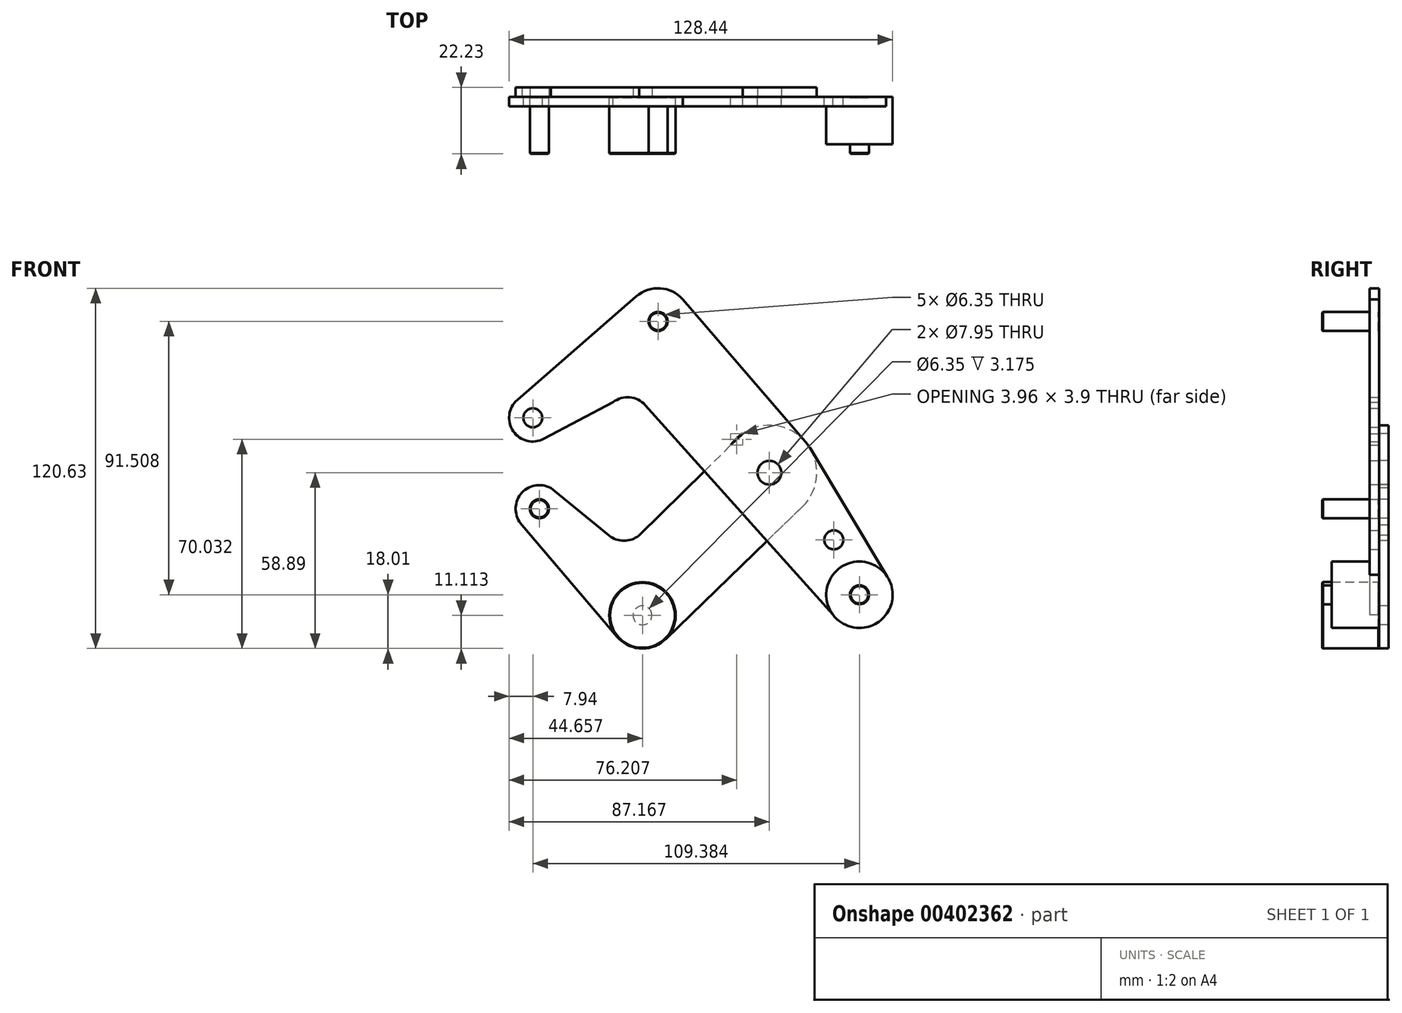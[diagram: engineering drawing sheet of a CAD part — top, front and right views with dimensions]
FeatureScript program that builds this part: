
annotation { "Feature Type Name" : "Feature", "Feature Type Description" : "" }
export const myFeature = defineFeature(function(context is Context, id is Id, definition is map)
    precondition{}
    {
        {
            var Q0;
            Q0=qCreatedBy(makeId("Front.planeOp"),FACE);
            var sketch = newSketch(context, id + "F0", { "sketchPlane" : qUnion([Q0])});
            skCircle(sketch, "E0", {"center": v(-13.62, 55.76) * mm, "radius": 11.11 * mm});
            skCircle(sketch, "E1", {"center": v(-55.55, 23.48) * mm, "radius": 7.94 * mm});
            skCircle(sketch, "E2", {"center": v(53.83, -35.75) * mm, "radius": 11.11 * mm});
            skCircle(sketch, "E3", {"center": v(23.68, 5.13) * mm, "radius": 15.88 * mm});
            skCircle(sketch, "E4", {"center": v(-55.55, 23.48) * mm, "radius": 3.18 * mm});
            skCircle(sketch, "E5", {"center": v(-13.62, 55.76) * mm, "radius": 3.18 * mm});
            skCircle(sketch, "E6", {"center": v(23.68, 5.13) * mm, "radius": 3.98 * mm});
            skCircle(sketch, "E7", {"center": v(23.68, 5.13) * mm, "radius": 3.18 * mm});
            skCircle(sketch, "E8", {"center": v(53.83, -35.75) * mm, "radius": 3.18 * mm});
            skCircle(sketch, "E9", {"center": v(45.26, -17.38) * mm, "radius": 3.18 * mm});
            skCircle(sketch, "E10", {"center": v(-18.83, -42.65) * mm, "radius": 11.11 * mm});
            skCircle(sketch, "E11", {"center": v(-53.36, -6.97) * mm, "radius": 7.94 * mm});
            skLineSegment(sketch, "E12", {"start": v(-60.76, 29.47) * mm, "end": v(-20.92, 64.14) * mm});
            skLineSegment(sketch, "E13", {"start": v(-59.17, -12.37) * mm, "end": v(-27.3, -49.85) * mm});
            skLineSegment(sketch, "E14", {"start": v(62.73, -29.1) * mm, "end": v(37.29, 13.3) * mm});
            skLineSegment(sketch, "E15", {"start": v(-5.31, 63.13) * mm, "end": v(35.7, 15.49) * mm});
            skLineSegment(sketch, "E16", {"start": v(44.9, -42.36) * mm, "end": v(12.34, -6.01) * mm});
            skLineSegment(sketch, "E17", {"start": v(-11.08, -50.6) * mm, "end": v(41.2, 0) * mm});
            skLineSegment(sketch, "E18", {"start": v(-49.56, 0) * mm, "end": v(-30.04, -15.9) * mm});
            skArc(sketch, "E19", {"start": v(-30.04, -15.9) * mm, "mid": v(-25.02, -17.69) * mm, "end": v(-20, -15.9) * mm});
            skLineSegment(sketch, "E20", {"start": v(-20, -15.9) * mm, "end": v(14.7, 18.22) * mm});
            skLineSegment(sketch, "E21", {"start": v(-17.87, 27.73) * mm, "end": v(12.34, -6.01) * mm});
            skArc(sketch, "E22", {"start": v(-17.87, 27.73) * mm, "mid": v(-23.07, 30.34) * mm, "end": v(-28.65, 28.72) * mm});
            skLineSegment(sketch, "E23", {"start": v(-28.65, 28.72) * mm, "end": v(-51.84, 16.46) * mm});
            skCircle(sketch, "E24", {"center": v(-53.36, -6.97) * mm, "radius": 3.18 * mm});
            skCircle(sketch, "E25", {"center": v(-18.83, -42.65) * mm, "radius": 3.18 * mm});
            skSolve(sketch);
        }
        {
            var Q0;
            Q0=qCreatedBy(makeId("Front.planeOp"),FACE);
            cPlane(context, id + "F1", {"entities" : qUnion([Q0]), "cplaneType" : CPlaneType.OFFSET, "offset" : 9.52 * mm, "width" : 152.4 * mm, "height" : 152.4 * mm});
        }
        {
            var Q0;
            {var subQ11=sQuery(id+"F0.wireOp",EDGE,"E12");Q0=makeQuery(id+"F0.imprint","IMPRINT",FACE,{"disambiguationData":[TD([[makeQuery(id+"F0.imprint","IMPRINT",EDGE,{"derivedFrom":subQ11}),-1.0]])]});}
            var Q1;
            Q1=makeQuery(id+"F0.imprint","IMPRINT",FACE,{"disambiguationData":[TD([[makeQuery(id+"F0.imprint","IMPRINT",EDGE,{"derivedFrom":sQuery(id+"F0.wireOp",EDGE,"E4")}),-1.0]])]});
            var Q2;
            Q2=makeQuery(id+"F0.imprint","IMPRINT",FACE,{"disambiguationData":[TD([[makeQuery(id+"F0.imprint","IMPRINT",EDGE,{"derivedFrom":sQuery(id+"F0.wireOp",EDGE,"E5")}),-1.0]])]});
            var Q3;
            Q3=makeQuery(id+"F0.imprint","IMPRINT",FACE,{"disambiguationData":[TD([[makeQuery(id+"F0.imprint","IMPRINT",EDGE,{"derivedFrom":sQuery(id+"F0.wireOp",EDGE,"E6")}),-1.0]])]});
            var Q4;
            {var subQ0=sQuery(id+"F0.wireOp",EDGE,"E17");var subQ1=sQuery(id+"F0.wireOp",EDGE,"E3");var subQ2=makeQuery(id+"F0.imprint","INTERSECT",VERTEX,{"derivedFrom":[subQ1,subQ0]});Q4=makeQuery(id+"F0.imprint","IMPRINT",FACE,{"disambiguationData":[TD([[makeQuery(id+"F0.imprint","IMPRINT",EDGE,{"disambiguationData":[TD([[subQ2,1.0]])],"derivedFrom":subQ1}),-1.0]])]});}
            var Q5;
            {var subQ0=sQuery(id+"F0.wireOp",EDGE,"E20");var subQ1=sQuery(id+"F0.wireOp",EDGE,"E3");var subQ2=makeQuery(id+"F0.imprint","INTERSECT",VERTEX,{"disambiguationData":[OD(1.0)],"derivedFrom":[subQ1,subQ0]});Q5=makeQuery(id+"F0.imprint","IMPRINT",FACE,{"disambiguationData":[TD([[makeQuery(id+"F0.imprint","IMPRINT",EDGE,{"disambiguationData":[TD([[subQ2,-1.0]])],"derivedFrom":subQ1}),-1.0]])]});}
            var Q6;
            Q6=makeQuery(id+"F0.imprint","IMPRINT",FACE,{"disambiguationData":[TD([[makeQuery(id+"F0.imprint","IMPRINT",EDGE,{"derivedFrom":sQuery(id+"F0.wireOp",EDGE,"E9")}),-1.0]])]});
            var Q7;
            Q7=makeQuery(id+"F0.imprint","IMPRINT",FACE,{"disambiguationData":[TD([[makeQuery(id+"F0.imprint","IMPRINT",EDGE,{"derivedFrom":sQuery(id+"F0.wireOp",EDGE,"E8")}),-1.0]])]});
            extrude(context, id + "F2", {"entities" : qUnion([Q0, Q1, Q2, Q3, Q4, Q5, Q6, Q7]), "depth" : 3.17 * mm});
        }
        {
            var Q0;
            Q0=makeQuery(id+"F0.imprint","IMPRINT",FACE,{"disambiguationData":[TD([[makeQuery(id+"F0.imprint","IMPRINT",EDGE,{"derivedFrom":sQuery(id+"F0.wireOp",EDGE,"E24")}),-1.0]])]});
            var Q1;
            Q1=makeQuery(id+"F0.imprint","IMPRINT",FACE,{"disambiguationData":[TD([[makeQuery(id+"F0.imprint","IMPRINT",EDGE,{"derivedFrom":sQuery(id+"F0.wireOp",EDGE,"E25")}),-1.0]])]});
            var Q2;
            {var subQ0=sQuery(id+"F0.wireOp",EDGE,"E13");Q2=makeQuery(id+"F0.imprint","IMPRINT",FACE,{"disambiguationData":[TD([[makeQuery(id+"F0.imprint","IMPRINT",EDGE,{"derivedFrom":subQ0}),1.0]])]});}
            var Q3;
            {var subQ0=sQuery(id+"F0.wireOp",EDGE,"E17");var subQ1=sQuery(id+"F0.wireOp",EDGE,"E3");var subQ2=makeQuery(id+"F0.imprint","INTERSECT",VERTEX,{"derivedFrom":[subQ1,subQ0]});Q3=makeQuery(id+"F0.imprint","IMPRINT",FACE,{"disambiguationData":[TD([[makeQuery(id+"F0.imprint","IMPRINT",EDGE,{"disambiguationData":[TD([[subQ2,1.0]])],"derivedFrom":subQ1}),-1.0]])]});}
            var Q4;
            Q4=makeQuery(id+"F0.imprint","IMPRINT",FACE,{"disambiguationData":[TD([[makeQuery(id+"F0.imprint","IMPRINT",EDGE,{"derivedFrom":sQuery(id+"F0.wireOp",EDGE,"E6")}),-1.0]])]});
            var Q5;
            {var subQ0=sQuery(id+"F0.wireOp",EDGE,"E20");var subQ1=sQuery(id+"F0.wireOp",EDGE,"E3");var subQ2=makeQuery(id+"F0.imprint","INTERSECT",VERTEX,{"disambiguationData":[OD(1.0)],"derivedFrom":[subQ1,subQ0]});Q5=makeQuery(id+"F0.imprint","IMPRINT",FACE,{"disambiguationData":[TD([[makeQuery(id+"F0.imprint","IMPRINT",EDGE,{"disambiguationData":[TD([[subQ2,-1.0]])],"derivedFrom":subQ1}),-1.0]])]});}
            extrude(context, id + "F3", {"entities" : qUnion([Q0, Q1, Q2, Q3, Q4, Q5]), "oppositeDirection" : true, "depth" : 3.17 * mm});
        }
        {
            var Q0;
            Q0=makeQuery(id+"F0.imprint","IMPRINT",FACE,{"disambiguationData":[TD([[makeQuery(id+"F0.imprint","IMPRINT",EDGE,{"derivedFrom":sQuery(id+"F0.wireOp",EDGE,"E8")}),1.0]])]});
            var Q1;
            Q1=makeQuery(id+"F0.imprint","IMPRINT",FACE,{"disambiguationData":[TD([[makeQuery(id+"F0.imprint","IMPRINT",EDGE,{"derivedFrom":sQuery(id+"F0.wireOp",EDGE,"E25")}),-1.0]])]});
            var Q2;
            Q2=makeQuery(id+"F0.imprint","IMPRINT",FACE,{"disambiguationData":[TD([[makeQuery(id+"F0.imprint","IMPRINT",EDGE,{"derivedFrom":sQuery(id+"F0.wireOp",EDGE,"E25")}),1.0]])]});
            var Q3;
            Q3=makeQuery(id+"F0.imprint","IMPRINT",FACE,{"disambiguationData":[TD([[makeQuery(id+"F0.imprint","IMPRINT",EDGE,{"derivedFrom":sQuery(id+"F0.wireOp",EDGE,"E24")}),1.0]])]});
            var Q4;
            Q4=makeQuery(id+"F0.imprint","IMPRINT",FACE,{"disambiguationData":[TD([[makeQuery(id+"F0.imprint","IMPRINT",EDGE,{"derivedFrom":sQuery(id+"F0.wireOp",EDGE,"E5")}),1.0]])]});
            var Q5;
            Q5=makeQuery(id+"F0.imprint","IMPRINT",FACE,{"disambiguationData":[TD([[makeQuery(id+"F0.imprint","IMPRINT",EDGE,{"derivedFrom":sQuery(id+"F0.wireOp",EDGE,"E8")}),-1.0]])]});
            var Q6;
            Q6=qCreatedBy(id+"F1.planeOp",FACE);
            extrude(context, id + "F4", {"entities" : qUnion([Q0, Q1, Q2, Q3, Q4, Q5]), "endBound" : BoundingType.UP_TO_SURFACE, "endBoundEntityFace" : qUnion([Q6]), "depth" : 25.4 * mm});
        }
        {
            var Q0;
            Q0=makeQuery(id+"F2.opExtrude","SWEPT_BODY",BODY,{"disambiguationData":[OSD([sQuery(id+"F0.wireOp",EDGE,"E0"),sQuery(id+"F0.wireOp",EDGE,"E1"),sQuery(id+"F0.wireOp",EDGE,"E2"),sQuery(id+"F0.wireOp",EDGE,"E3"),sQuery(id+"F0.wireOp",EDGE,"E4"),sQuery(id+"F0.wireOp",EDGE,"E5"),sQuery(id+"F0.wireOp",EDGE,"E6"),sQuery(id+"F0.wireOp",EDGE,"E8"),sQuery(id+"F0.wireOp",EDGE,"E9"),sQuery(id+"F0.wireOp",EDGE,"E12"),sQuery(id+"F0.wireOp",EDGE,"E14"),sQuery(id+"F0.wireOp",EDGE,"E15"),sQuery(id+"F0.wireOp",EDGE,"E16"),sQuery(id+"F0.wireOp",EDGE,"E20"),sQuery(id+"F0.wireOp",EDGE,"E21"),sQuery(id+"F0.wireOp",EDGE,"E22"),sQuery(id+"F0.wireOp",EDGE,"E23")])]});
            var Q1;
            Q1=makeQuery(id+"F3.opExtrude","SWEPT_BODY",BODY,{"disambiguationData":[OSD([sQuery(id+"F0.wireOp",EDGE,"E3"),sQuery(id+"F0.wireOp",EDGE,"E6"),sQuery(id+"F0.wireOp",EDGE,"E10"),sQuery(id+"F0.wireOp",EDGE,"E11"),sQuery(id+"F0.wireOp",EDGE,"E13"),sQuery(id+"F0.wireOp",EDGE,"E17"),sQuery(id+"F0.wireOp",EDGE,"E18"),sQuery(id+"F0.wireOp",EDGE,"E19"),sQuery(id+"F0.wireOp",EDGE,"E20"),sQuery(id+"F0.wireOp",EDGE,"E24"),sQuery(id+"F0.wireOp",EDGE,"E25")])]});
            var Q2;
            Q2=makeQuery(id+"F4.opExtrude","SWEPT_BODY",BODY,{"disambiguationData":[OSD([sQuery(id+"F0.wireOp",EDGE,"E5")])]});
            var Q3;
            Q3=makeQuery(id+"F4.opExtrude","SWEPT_BODY",BODY,{"disambiguationData":[OSD([sQuery(id+"F0.wireOp",EDGE,"E10")])]});
            var Q4;
            Q4=makeQuery(id+"F4.opExtrude","SWEPT_BODY",BODY,{"disambiguationData":[OSD([sQuery(id+"F0.wireOp",EDGE,"E2")])]});
            var Q5;
            Q5=makeQuery(id+"F4.opExtrude","SWEPT_BODY",BODY,{"disambiguationData":[OSD([sQuery(id+"F0.wireOp",EDGE,"E24")])]});
            booleanBodies(context, id + "F5", {"operationType" : BooleanOperationType.SUBTRACTION, "tools" : qUnion([Q0, Q1]), "targets" : qUnion([Q2, Q3, Q4, Q5]), "keepTools" : true});
        }
        {
            var Q0;
            Q0=makeQuery(id+"F4.opExtrude","CAP_FACE",FACE,{"disambiguationData":[OSD([sQuery(id+"F0.wireOp",EDGE,"E2")])],"isStart":true});
            var Q1;
            Q1=makeQuery(id+"F4.opExtrude","CAP_EDGE",EDGE,{"disambiguationData":[OSD([sQuery(id+"F0.wireOp",EDGE,"E5")])],"isStart":true});
            var Q2;
            Q2=makeQuery(id+"F4.opExtrude","CAP_EDGE",EDGE,{"disambiguationData":[OSD([sQuery(id+"F0.wireOp",EDGE,"E24")])],"isStart":true});
            var Q3;
            Q3=makeQuery(id+"F4.opExtrude","CAP_FACE",FACE,{"disambiguationData":[OSD([sQuery(id+"F0.wireOp",EDGE,"E10")])],"isStart":true});
            chamfer(context, id + "F6", {"entities" : qUnion([Q0, Q1, Q2, Q3]), "width" : 0.25 * mm, "tangentPropagation" : true});
        }
        {
            var Q0;
            Q0=makeQuery(id+"F4.opExtrude","SWEPT_BODY",BODY,{"disambiguationData":[OSD([sQuery(id+"F0.wireOp",EDGE,"E24")])]});
            var Q1;
            Q1=makeQuery(id+"F4.opExtrude","SWEPT_BODY",BODY,{"disambiguationData":[OSD([sQuery(id+"F0.wireOp",EDGE,"E5")])]});
            var Q2;
            Q2=makeQuery(id+"F4.opExtrude","SWEPT_BODY",BODY,{"disambiguationData":[OSD([sQuery(id+"F0.wireOp",EDGE,"E2")])]});
            var Q3;
            Q3=makeQuery(id+"F4.opExtrude","SWEPT_BODY",BODY,{"disambiguationData":[OSD([sQuery(id+"F0.wireOp",EDGE,"E10")])]});
            var Q4;
            Q4=qCreatedBy(id+"F1.planeOp",FACE);
            mirror(context, id + "F7", {"operationType" : NewBodyOperationType.ADD, "entities" : qUnion([Q0, Q1, Q2, Q3]), "mirrorPlane" : qUnion([Q4])});
        }
    });
